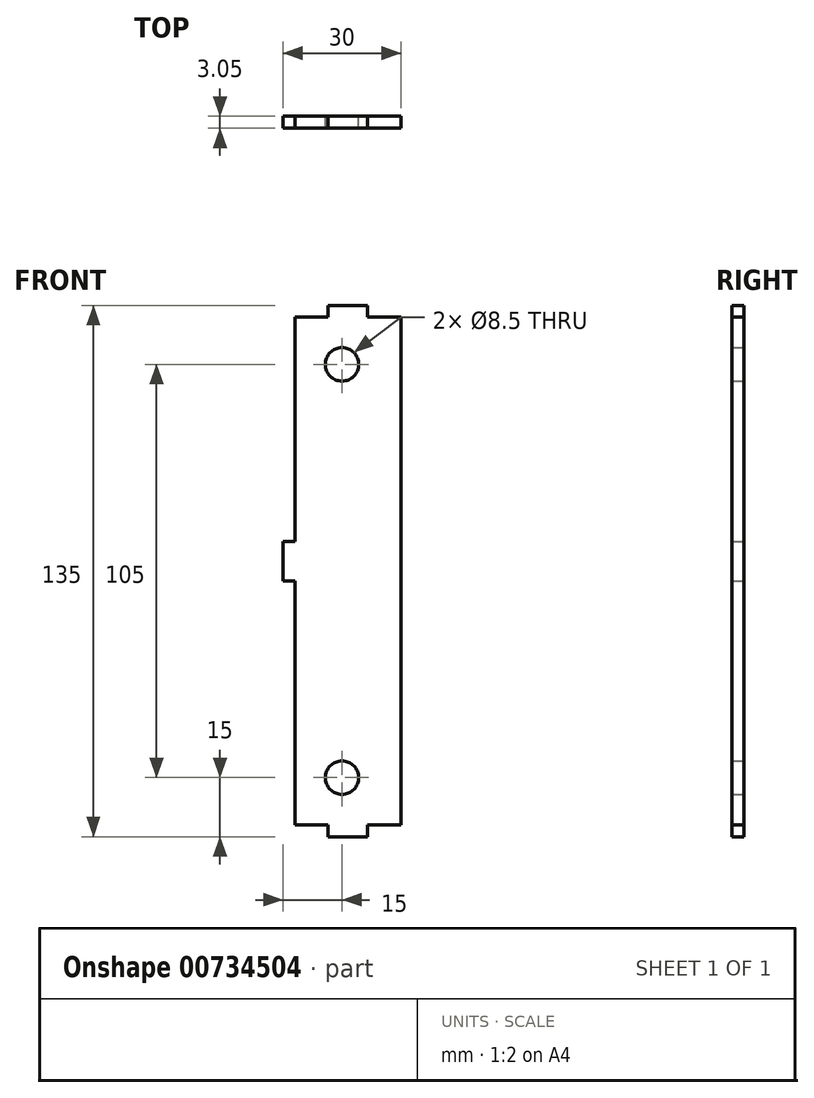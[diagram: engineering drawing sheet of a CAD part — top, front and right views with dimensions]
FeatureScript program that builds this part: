
annotation { "Feature Type Name" : "Feature", "Feature Type Description" : "" }
export const myFeature = defineFeature(function(context is Context, id is Id, definition is map)
    precondition{}
    {
        {
            var Q0;
            Q0=qCreatedBy(makeId("Front.planeOp"),FACE);
            var sketch = newSketch(context, id + "F0", { "sketchPlane" : qUnion([Q0])});
            skLineSegment(sketch, "E0", {"start": v(-12, 7.5) * mm, "end": v(-12, 64.5) * mm});
            skLineSegment(sketch, "E1", {"start": v(-12, 64.5) * mm, "end": v(-3.5, 64.5) * mm});
            skLineSegment(sketch, "E2", {"start": v(-3.5, 64.5) * mm, "end": v(-3.5, 67.5) * mm});
            skLineSegment(sketch, "E3", {"start": v(-3.5, 67.5) * mm, "end": v(6.5, 67.5) * mm});
            skLineSegment(sketch, "E4", {"start": v(6.5, 67.5) * mm, "end": v(6.5, 64.5) * mm});
            skLineSegment(sketch, "E5", {"start": v(6.5, 64.5) * mm, "end": v(15, 64.5) * mm});
            skLineSegment(sketch, "E6", {"start": v(15, 64.5) * mm, "end": v(15, -64.5) * mm});
            skLineSegment(sketch, "E7", {"start": v(15, -64.5) * mm, "end": v(6.5, -64.5) * mm});
            skLineSegment(sketch, "E8", {"start": v(6.5, -64.5) * mm, "end": v(6.5, -67.5) * mm});
            skLineSegment(sketch, "E9", {"start": v(6.5, -67.5) * mm, "end": v(-3.5, -67.5) * mm});
            skLineSegment(sketch, "E10", {"start": v(-3.5, -67.5) * mm, "end": v(-3.5, -64.5) * mm});
            skLineSegment(sketch, "E11", {"start": v(-3.5, -64.5) * mm, "end": v(-12, -64.5) * mm});
            skLineSegment(sketch, "E12", {"start": v(-12, -64.5) * mm, "end": v(-12, -2.5) * mm});
            skLineSegment(sketch, "E13", {"start": v(-12, -2.5) * mm, "end": v(-15, -2.5) * mm});
            skLineSegment(sketch, "E14", {"start": v(-15, -2.5) * mm, "end": v(-15, 7.5) * mm});
            skLineSegment(sketch, "E15", {"start": v(-15, 7.5) * mm, "end": v(-12, 7.5) * mm});
            skCircle(sketch, "E16", {"center": v(0, -52.5) * mm, "radius": 4.25 * mm});
            skCircle(sketch, "E17", {"center": v(0, 52.5) * mm, "radius": 4.25 * mm});
            skSolve(sketch);
        }
        {
            var Q0;
            Q0 = qSketchRegion(id + "F0", true);
            extrude(context, id + "F1", {"entities" : qUnion([Q0]), "depth" : 3.05 * mm, "offsetDistance" : 25.4 * mm});
        }
    });
